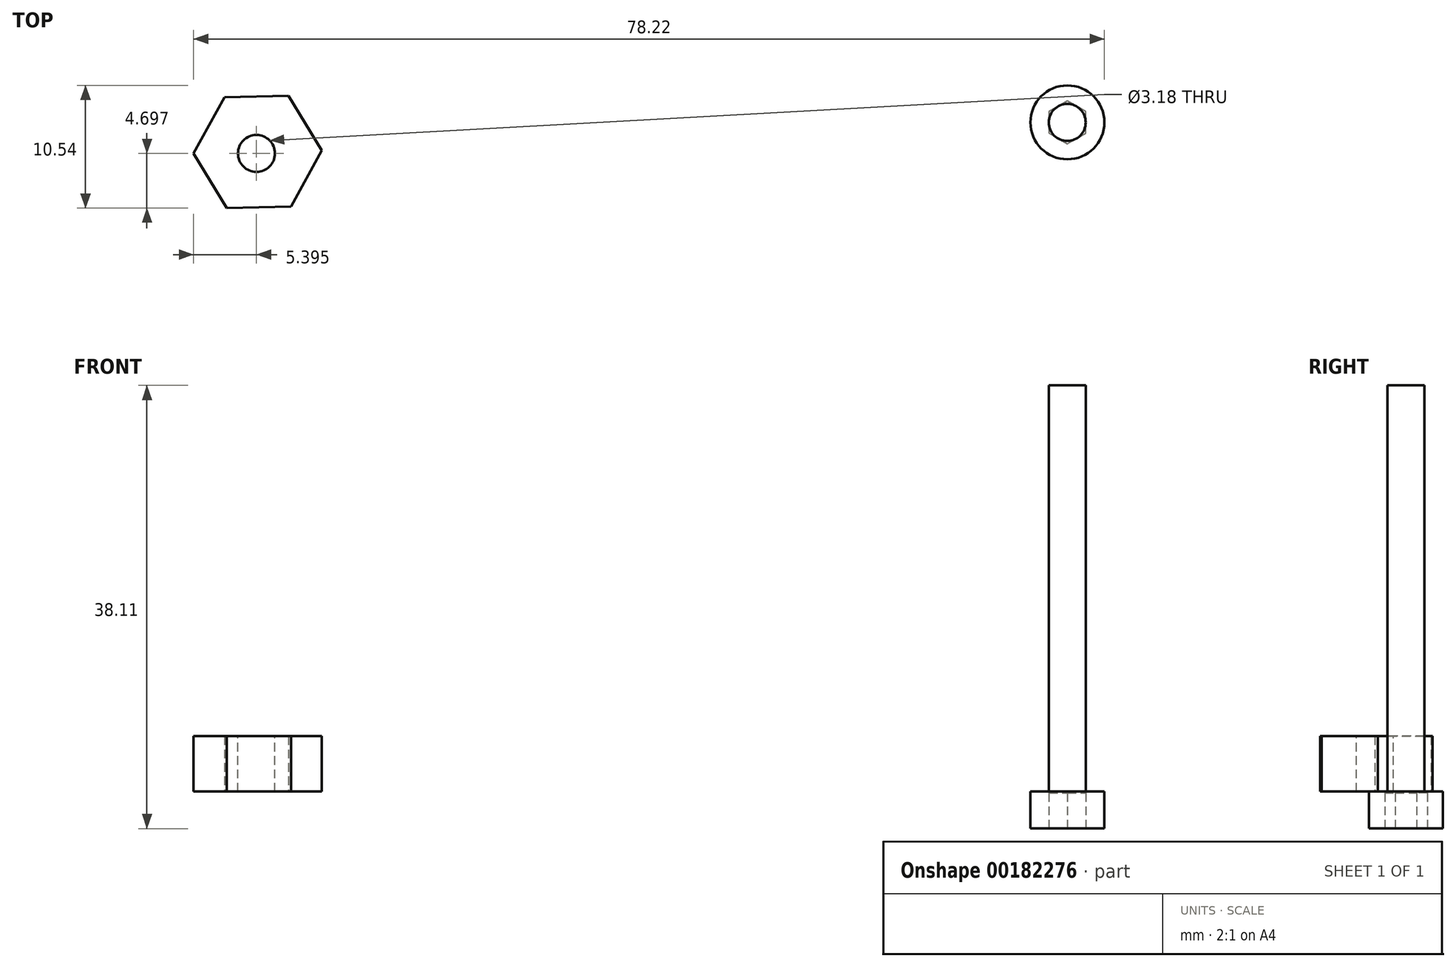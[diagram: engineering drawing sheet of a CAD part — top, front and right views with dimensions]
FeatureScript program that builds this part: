
annotation { "Feature Type Name" : "Feature", "Feature Type Description" : "" }
export const myFeature = defineFeature(function(context is Context, id is Id, definition is map)
    precondition{}
    {
        {
            var Q0;
            Q0=qCreatedBy(makeId("Top.planeOp"),FACE);
            var sketch = newSketch(context, id + "F0", { "sketchPlane" : qUnion([Q0])});
            skCircle(sketch, "E0.cCircle", {"center": v(-31.73, 40.84) * mm, "radius": 4.76 * mm, "construction": true});
            skLineSegment(sketch, "E0.0", {"start": v(-26.23, 40.96) * mm, "end": v(-28.88, 36.14) * mm});
            skLineSegment(sketch, "E0.1", {"start": v(-28.88, 36.14) * mm, "end": v(-34.37, 36.02) * mm});
            skLineSegment(sketch, "E0.2", {"start": v(-34.37, 36.02) * mm, "end": v(-37.23, 40.72) * mm});
            skLineSegment(sketch, "E0.3", {"start": v(-37.23, 40.72) * mm, "end": v(-34.58, 45.54) * mm});
            skLineSegment(sketch, "E0.4", {"start": v(-34.58, 45.54) * mm, "end": v(-29.09, 45.66) * mm});
            skLineSegment(sketch, "E0.5", {"start": v(-29.09, 45.66) * mm, "end": v(-26.23, 40.96) * mm});
            skPoint(sketch, "E0.0.midPoint", {"position": v(-27.55, 38.55) * mm});
            skSolve(sketch);
        }
        {
            var Q0;
            Q0=makeQuery(id+"F0.imprint","IMPRINT",FACE,{"disambiguationData":[TD([[makeQuery(id+"F0.imprint","IMPRINT",EDGE,{"derivedFrom":sQuery(id+"F0.wireOp",EDGE,"E0.0")}),-1.0]])]});
            extrude(context, id + "F1", {"entities" : qUnion([Q0]), "depth" : 4.76 * mm});
        }
        {
            var Q0;
            Q0=makeQuery(id+"F1.opExtrude","CAP_FACE",FACE,{"disambiguationData":[OSD([sQuery(id+"F0.wireOp",EDGE,"E0.0"),sQuery(id+"F0.wireOp",EDGE,"E0.1"),sQuery(id+"F0.wireOp",EDGE,"E0.2"),sQuery(id+"F0.wireOp",EDGE,"E0.3"),sQuery(id+"F0.wireOp",EDGE,"E0.4"),sQuery(id+"F0.wireOp",EDGE,"E0.5")])],"isStart":false});
            var sketch = newSketch(context, id + "F2", { "sketchPlane" : qUnion([Q0])});
            skCircle(sketch, "E1", {"center": v(-31.83, 40.72) * mm, "radius": 1.59 * mm});
            skPoint(sketch, "E1.centerSnap0", {"position": v(-31.83, 45.6) * mm});
            skSolve(sketch);
        }
        {
            var Q0;
            Q0=makeQuery(id+"F2.imprint","IMPRINT",FACE,{"disambiguationData":[TD([[makeQuery(id+"F2.imprint","IMPRINT",EDGE,{"derivedFrom":sQuery(id+"F2.wireOp",EDGE,"E1")}),1.0]])]});
            extrude(context, id + "F3", {"entities" : qUnion([Q0]), "operationType" : NewBodyOperationType.REMOVE, "oppositeDirection" : true, "depth" : 4.76 * mm});
        }
        {
            var Q0;
            Q0=qCreatedBy(makeId("Top.planeOp"),FACE);
            var sketch = newSketch(context, id + "F4", { "sketchPlane" : qUnion([Q0])});
            skCircle(sketch, "E2", {"center": v(37.82, 43.38) * mm, "radius": 3.18 * mm});
            skSolve(sketch);
        }
        {
            var Q0;
            Q0=makeQuery(id+"F4.imprint","IMPRINT",FACE,{"disambiguationData":[TD([[makeQuery(id+"F4.imprint","IMPRINT",EDGE,{"derivedFrom":sQuery(id+"F4.wireOp",EDGE,"E2")}),1.0]])]});
            var sketch = newSketch(context, id + "F5", { "sketchPlane" : qUnion([Q0])});
            skCircle(sketch, "E3", {"center": v(37.8, 43.38) * mm, "radius": 1.59 * mm});
            skSolve(sketch);
        }
        {
            var Q0;
            Q0=makeQuery(id+"F5.imprint","IMPRINT",FACE,{"disambiguationData":[TD([[makeQuery(id+"F5.imprint","IMPRINT",EDGE,{"derivedFrom":sQuery(id+"F5.wireOp",EDGE,"E3")}),1.0]])]});
            extrude(context, id + "F6", {"entities" : qUnion([Q0]), "depth" : 34.92 * mm});
        }
        {
            var Q0;
            Q0=makeQuery(id+"F4.imprint","IMPRINT",FACE,{"disambiguationData":[TD([[makeQuery(id+"F4.imprint","IMPRINT",EDGE,{"derivedFrom":sQuery(id+"F4.wireOp",EDGE,"E2")}),1.0]])]});
            extrude(context, id + "F7", {"entities" : qUnion([Q0]), "operationType" : NewBodyOperationType.ADD, "oppositeDirection" : true, "depth" : 3.17 * mm});
        }
        {
            var Q0;
            Q0=makeQuery(id+"F7.opExtrude","CAP_FACE",FACE,{"disambiguationData":[OSD([sQuery(id+"F4.wireOp",EDGE,"E2")])],"isStart":false});
            var sketch = newSketch(context, id + "F8", { "sketchPlane" : qUnion([Q0])});
            skCircle(sketch, "E4.cCircle", {"center": v(37.82, -43.38) * mm, "radius": 1.59 * mm, "construction": true});
            skLineSegment(sketch, "E4.0", {"start": v(39.4, -42.47) * mm, "end": v(39.4, -44.3) * mm});
            skLineSegment(sketch, "E4.1", {"start": v(39.4, -44.3) * mm, "end": v(37.82, -45.22) * mm});
            skLineSegment(sketch, "E4.2", {"start": v(37.82, -45.22) * mm, "end": v(36.23, -44.3) * mm});
            skLineSegment(sketch, "E4.3", {"start": v(36.23, -44.3) * mm, "end": v(36.23, -42.47) * mm});
            skLineSegment(sketch, "E4.4", {"start": v(36.23, -42.47) * mm, "end": v(37.82, -41.55) * mm});
            skLineSegment(sketch, "E4.5", {"start": v(37.82, -41.55) * mm, "end": v(39.4, -42.47) * mm});
            skPoint(sketch, "E4.0.midPoint", {"position": v(39.4, -43.38) * mm});
            skSolve(sketch);
        }
        {
            var Q0;
            Q0=makeQuery(id+"F8.imprint","IMPRINT",FACE,{"disambiguationData":[TD([[makeQuery(id+"F8.imprint","IMPRINT",EDGE,{"derivedFrom":sQuery(id+"F8.wireOp",EDGE,"E4.0")}),-1.0]])]});
            extrude(context, id + "F9", {"entities" : qUnion([Q0]), "operationType" : NewBodyOperationType.REMOVE, "oppositeDirection" : true, "depth" : 3.05 * mm});
        }
    });
